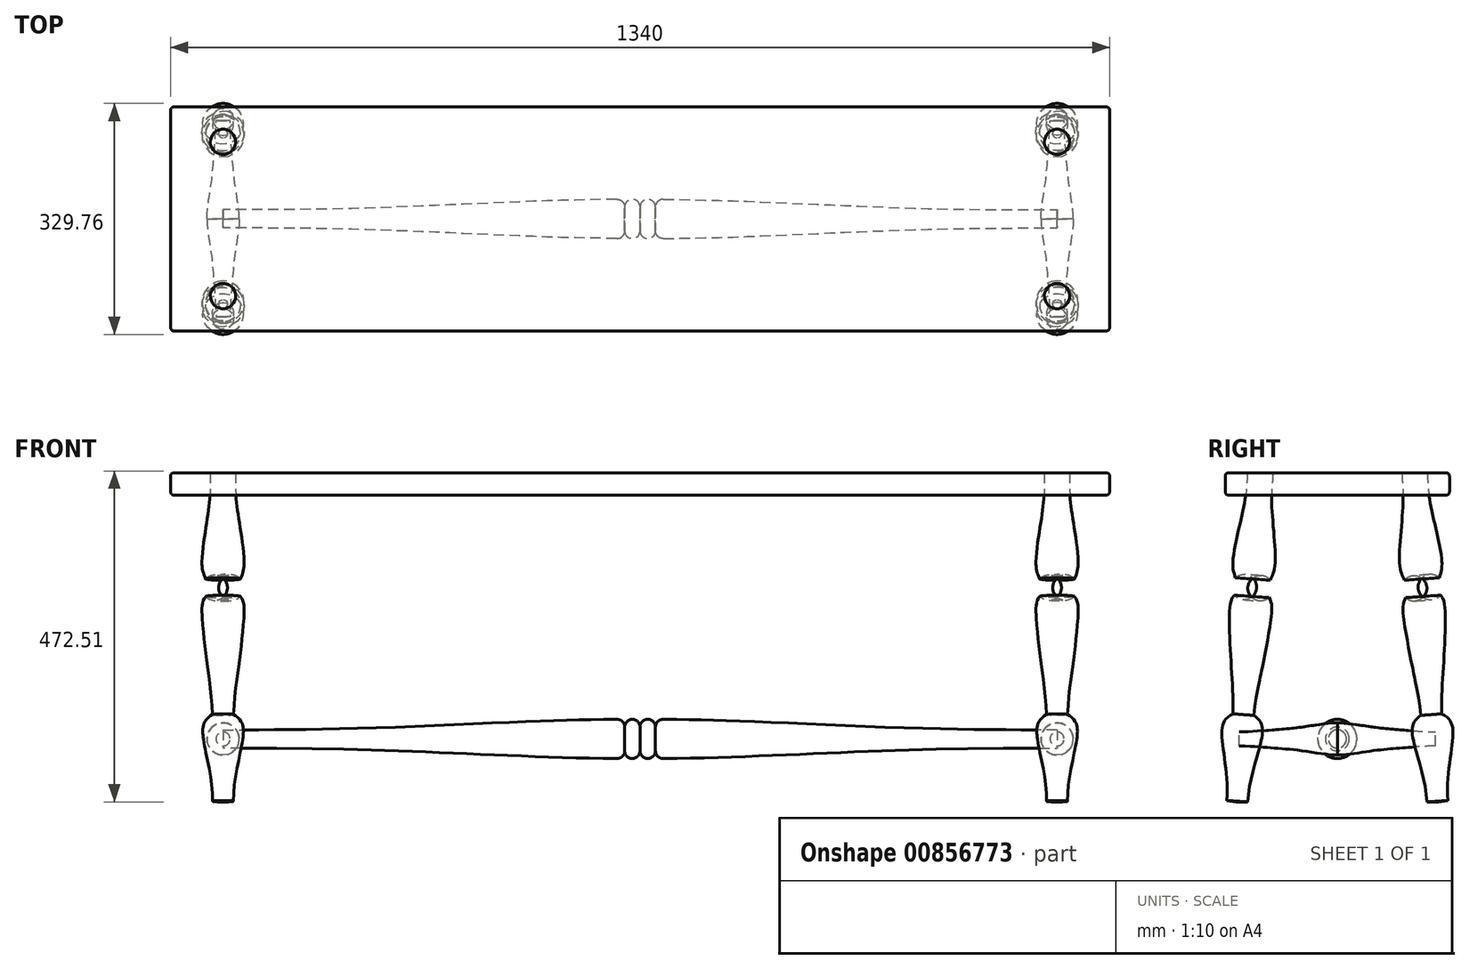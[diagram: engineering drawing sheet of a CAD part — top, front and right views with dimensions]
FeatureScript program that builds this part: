
annotation { "Feature Type Name" : "Feature", "Feature Type Description" : "" }
export const myFeature = defineFeature(function(context is Context, id is Id, definition is map)
    precondition{}
    {
        {
            assignVariable(context, id + "F0", {"name" : "height", "anyValue" : 470});
        }
        {
            assignVariable(context, id + "F1", {"name" : "topThick", "anyValue" : 32});
        }
        {
            assignVariable(context, id + "F2", {"name" : "endOverhang", "anyValue" : 75});
        }
        {
            var Q0;
            Q0=qCreatedBy(makeId("Top.planeOp"),FACE);
            cPlane(context, id + "F3", {"entities" : qUnion([Q0]), "cplaneType" : CPlaneType.OFFSET, "offset" : (getVariable(context, 'height')) * mm, "width" : 150 * mm, "height" : 150 * mm});
        }
        {
            var Q0;
            Q0=qCreatedBy(id+"F3.planeOp",FACE);
            var sketch = newSketch(context, id + "F4", { "sketchPlane" : qUnion([Q0])});
            skLineSegment(sketch, "E0.bottom", {"start": v(670, 160) * mm, "end": v(-670, 160) * mm});
            skLineSegment(sketch, "E0.top", {"start": v(670, -160) * mm, "end": v(-670, -160) * mm});
            skLineSegment(sketch, "E0.left", {"start": v(670, 160) * mm, "end": v(670, -160) * mm});
            skLineSegment(sketch, "E0.right", {"start": v(-670, 160) * mm, "end": v(-670, -160) * mm});
            skPoint(sketch, "E0.middle", {"position": v(0, 0) * mm});
            skSolve(sketch);
        }
        {
            var Q0;
            Q0=qSketchRegion(id+"F4",true);
            extrude(context, id + "F5", {"entities" : qUnion([Q0]), "oppositeDirection" : true, "depth" : (getVariable(context, 'topThick')) * mm, "offsetDistance" : 25 * mm});
        }
        {
            var Q0;
            Q0=makeQuery(id+"F5.opExtrude","CAP_FACE",FACE,{"disambiguationData":[OSD([sQuery(id+"F4.wireOp",EDGE,"E0.bottom"),sQuery(id+"F4.wireOp",EDGE,"E0.top"),sQuery(id+"F4.wireOp",EDGE,"E0.left"),sQuery(id+"F4.wireOp",EDGE,"E0.right")])],"isStart":true});
            var Q1;
            Q1=makeQuery(id+"F5.opExtrude","SWEPT_FACE",FACE,{"disambiguationData":[OSD([sQuery(id+"F4.wireOp",EDGE,"E0.left")])]});
            var Q2;
            Q2=makeQuery(id+"F5.opExtrude","SWEPT_FACE",FACE,{"disambiguationData":[OSD([sQuery(id+"F4.wireOp",EDGE,"E0.right")])]});
            var Q3;
            Q3=makeQuery(id+"F5.opExtrude","CAP_FACE",FACE,{"disambiguationData":[OSD([sQuery(id+"F4.wireOp",EDGE,"E0.bottom"),sQuery(id+"F4.wireOp",EDGE,"E0.top"),sQuery(id+"F4.wireOp",EDGE,"E0.left"),sQuery(id+"F4.wireOp",EDGE,"E0.right")])],"isStart":false});
            fillet(context, id + "F6", {"entities" : qUnion([Q0, Q1, Q2, Q3]), "radius" : 5 * mm, "tangentPropagation" : true, "allowEdgeOverflow" : false});
        }
        {
            var Q0;
            Q0=makeQuery(id+"F5.opExtrude","SWEPT_FACE",FACE,{"disambiguationData":[OSD([sQuery(id+"F4.wireOp",EDGE,"E0.left")])]});
            cPlane(context, id + "F7", {"entities" : qUnion([Q0]), "cplaneType" : CPlaneType.OFFSET, "offset" : (getVariable(context, 'endOverhang')) * mm, "oppositeDirection" : true, "width" : 150 * mm, "height" : 150 * mm});
        }
        {
            var Q0;
            Q0=qCreatedBy(id+"F7.planeOp",FACE);
            var sketch = newSketch(context, id + "F8", { "sketchPlane" : qUnion([Q0])});
            skLineSegment(sketch, "E1", {"start": v(-110, 470) * mm, "end": v(-142.87, 0) * mm});
            skLineSegment(sketch, "E2.0", {"start": v(-81.45, 448.19) * mm, "end": v(-112.8, 0) * mm, "construction": true});
            skLineSegment(sketch, "E3", {"start": v(-110, 528.62) * mm, "end": v(-110, 470) * mm, "construction": true});
            skPoint(sketch, "E4", {"position": v(-92, 470) * mm});
            skLineSegment(sketch, "E5", {"start": v(-95.66, 316.63) * mm, "end": v(-120.6, 318.37) * mm, "construction": true});
            skLineSegment(sketch, "E6", {"start": v(-122.35, 293.43) * mm, "end": v(-97.4, 291.69) * mm, "construction": true});
            skLineSegment(sketch, "E7", {"start": v(-119.2, 338.32) * mm, "end": v(-89.2, 336.22) * mm, "construction": true});
            skFitSpline(sketch, "E8", {"points": [v(-92, 470) * mm, v(-93.84, 428.77) * mm, v(-89.2, 336.22) * mm, v(-95.66, 316.63) * mm], "startDerivative": vector(-1.33, -110.65) * mm, "endDerivative": vector(-26.5, -67.26) * mm});
            skArc(sketch, "E9", {"start": v(-97.4, 291.69) * mm, "mid": v(-91.55, 303.8) * mm, "end": v(-95.66, 316.63) * mm});
            skPoint(sketch, "E10", {"position": v(-127.87, 0) * mm});
            skLineSegment(sketch, "E11", {"start": v(-142.87, 0) * mm, "end": v(-127.87, 0) * mm});
            skLineSegment(sketch, "E12", {"start": v(-135.89, 99.76) * mm, "end": v(-106.96, 97.73) * mm, "construction": true});
            skLineSegment(sketch, "E13", {"start": v(-119.18, 123.65) * mm, "end": v(-134.15, 124.7) * mm, "construction": true});
            skFitSpline(sketch, "E14", {"points": [v(-119.18, 123.65) * mm, v(-106.96, 97.73) * mm, v(-127.87, 0) * mm], "startDerivative": vector(88.45, -61.4) * mm, "endDerivative": vector(-11.95, -183.7) * mm});
            skLineSegment(sketch, "E15", {"start": v(-124.1, 268.5) * mm, "end": v(-94.16, 266.4) * mm, "construction": true});
            skFitSpline(sketch, "E16", {"points": [v(-97.4, 291.69) * mm, v(-94.16, 266.4) * mm, v(-106.08, 197.69) * mm, v(-119.18, 123.65) * mm], "startDerivative": vector(58.5, -103.3) * mm, "endDerivative": vector(-23.38, -210.4) * mm});
            skLineSegment(sketch, "E17", {"start": v(-110, 470) * mm, "end": v(-92, 470) * mm});
            skLineSegment(sketch, "E18", {"start": v(-93.84, 428.77) * mm, "end": v(-112.8, 430.1) * mm, "construction": true});
            skSolve(sketch);
        }
        {
            var Q0;
            Q0=qSketchRegion(id+"F8",true);
            var Q1;
            Q1=sQuery(id+"F8.wireOp",EDGE,"E1");
            revolve(context, id + "F9", {"entities" : qUnion([Q0]), "axis" : qUnion([Q1]), "revolveType" : RevolveType.FULL});
        }
        {
            var Q0;
            Q0=qCreatedBy(id+"F7.planeOp",FACE);
            var sketch = newSketch(context, id + "F10", { "sketchPlane" : qUnion([Q0])});
            skLineSegment(sketch, "E19.bottom", {"start": v(-133.48, 475.27) * mm, "end": v(-82.36, 475.27) * mm});
            skLineSegment(sketch, "E19.top", {"start": v(-133.48, 470) * mm, "end": v(-82.36, 470) * mm});
            skLineSegment(sketch, "E19.left", {"start": v(-133.48, 475.27) * mm, "end": v(-133.48, 470) * mm});
            skLineSegment(sketch, "E19.right", {"start": v(-82.36, 475.27) * mm, "end": v(-82.36, 470) * mm});
            skSolve(sketch);
        }
        {
            var Q0;
            Q0=makeQuery(id+"F10.imprint","IMPRINT",FACE,{"disambiguationData":[TD([[makeQuery(id+"F10.imprint","IMPRINT",EDGE,{"derivedFrom":sQuery(id+"F10.wireOp",EDGE,"E19.bottom")}),-1.0]])]});
            extrude(context, id + "F11", {"entities" : qUnion([Q0]), "operationType" : NewBodyOperationType.REMOVE, "endBound" : BoundingType.THROUGH_ALL, "oppositeDirection" : true, "depth" : 25 * mm, "offsetDistance" : 25 * mm, "hasSecondDirection" : true, "secondDirectionOppositeDirection" : false, "secondDirectionDepth" : 25 * mm});
        }
        {
            var Q0;
            Q0=makeQuery(id+"F9.opRevolve","SWEPT_BODY",BODY,{"disambiguationData":[OSD([sQuery(id+"F8.wireOp",EDGE,"E1"),sQuery(id+"F8.wireOp",EDGE,"E8"),sQuery(id+"F8.wireOp",EDGE,"E9"),sQuery(id+"F8.wireOp",EDGE,"E11"),sQuery(id+"F8.wireOp",EDGE,"E14"),sQuery(id+"F8.wireOp",EDGE,"E16"),sQuery(id+"F8.wireOp",EDGE,"E17")])]});
            var Q1;
            Q1=qCreatedBy(makeId("Front.planeOp"),FACE);
            mirror(context, id + "F12", {"entities" : qUnion([Q0]), "mirrorPlane" : qUnion([Q1])});
        }
        {
            var Q0;
            Q0=qCreatedBy(id+"F7.planeOp",FACE);
            var sketch = newSketch(context, id + "F13", { "sketchPlane" : qUnion([Q0])});
            skLineSegment(sketch, "E20", {"start": v(-140, 90) * mm, "end": v(140, 90) * mm});
            skLineSegment(sketch, "E21", {"start": v(-140, 90) * mm, "end": v(-140, 80) * mm});
            skLineSegment(sketch, "E22", {"start": v(140, 90) * mm, "end": v(140, 80) * mm});
            skFitSpline(sketch, "E23", {"points": [v(-140, 80) * mm, v(-90, 77) * mm, v(-50, 73) * mm, v(0, 67) * mm], "startDerivative": vector(196.9, -5.62) * mm, "endDerivative": vector(98.9, 2.93) * mm});
            skFitSpline(sketch, "E24.MirrorCS", {"points": [v(140, 80) * mm, v(90, 77) * mm, v(50, 73) * mm, v(0, 67) * mm], "startDerivative": vector(-196.9, -5.62) * mm, "endDerivative": vector(-98.9, 2.93) * mm});
            skLineSegment(sketch, "E25", {"start": v(0, 67) * mm, "end": v(0, 90) * mm, "construction": true});
            skLineSegment(sketch, "E26", {"start": v(-90, 77) * mm, "end": v(-90, 90) * mm, "construction": true});
            skLineSegment(sketch, "E27", {"start": v(-50, 73) * mm, "end": v(-50, 90) * mm, "construction": true});
            skSolve(sketch);
        }
        {
            var Q0;
            Q0=makeQuery(id+"F13.imprint","IMPRINT",FACE,{"disambiguationData":[TD([[makeQuery(id+"F13.imprint","IMPRINT",EDGE,{"derivedFrom":sQuery(id+"F13.wireOp",EDGE,"E20")}),-1.0]])]});
            var Q1;
            Q1=sQuery(id+"F13.wireOp",EDGE,"E20");
            revolve(context, id + "F14", {"entities" : qUnion([Q0]), "axis" : qUnion([Q1]), "revolveType" : RevolveType.FULL});
        }
        {
            var Q0;
            Q0=makeQuery(id+"F14.opRevolve","SWEPT_BODY",BODY,{"disambiguationData":[OSD([sQuery(id+"F13.wireOp",EDGE,"E20"),sQuery(id+"F13.wireOp",EDGE,"E21"),sQuery(id+"F13.wireOp",EDGE,"E22"),sQuery(id+"F13.wireOp",EDGE,"E23"),sQuery(id+"F13.wireOp",EDGE,"E24.MirrorCS")])]});
            var Q1;
            Q1=makeQuery(id+"F9.opRevolve","SWEPT_BODY",BODY,{"disambiguationData":[OSD([sQuery(id+"F8.wireOp",EDGE,"E1"),sQuery(id+"F8.wireOp",EDGE,"E8"),sQuery(id+"F8.wireOp",EDGE,"E9"),sQuery(id+"F8.wireOp",EDGE,"E11"),sQuery(id+"F8.wireOp",EDGE,"E14"),sQuery(id+"F8.wireOp",EDGE,"E16"),sQuery(id+"F8.wireOp",EDGE,"E17")])]});
            var Q2;
            Q2=makeQuery(id+"F12.opPattern","COPY",BODY,{"derivedFrom":makeQuery(id+"F9.opRevolve","SWEPT_BODY",BODY,{"disambiguationData":[OSD([sQuery(id+"F8.wireOp",EDGE,"E1"),sQuery(id+"F8.wireOp",EDGE,"E8"),sQuery(id+"F8.wireOp",EDGE,"E9"),sQuery(id+"F8.wireOp",EDGE,"E11"),sQuery(id+"F8.wireOp",EDGE,"E14"),sQuery(id+"F8.wireOp",EDGE,"E16"),sQuery(id+"F8.wireOp",EDGE,"E17")])]}),"instanceName":"1"});
            var Q3;
            Q3=qCreatedBy(makeId("Right.planeOp"),FACE);
            mirror(context, id + "F15", {"entities" : qUnion([Q0, Q1, Q2]), "mirrorPlane" : qUnion([Q3])});
        }
        {
            var Q0;
            Q0=qCreatedBy(makeId("Front.planeOp"),FACE);
            var sketch = newSketch(context, id + "F16", { "sketchPlane" : qUnion([Q0])});
            skLineSegment(sketch, "E28", {"start": v(-595, 90) * mm, "end": v(595, 90) * mm});
            skLineSegment(sketch, "E29", {"start": v(595, 90) * mm, "end": v(595, 77) * mm});
            skLineSegment(sketch, "E30", {"start": v(-595, 90) * mm, "end": v(-595, 77) * mm});
            skLineSegment(sketch, "E31", {"start": v(0, 90) * mm, "end": v(0, 62) * mm, "construction": true});
            skLineSegment(sketch, "E32", {"start": v(-154, 90) * mm, "end": v(-154, 65) * mm, "construction": true});
            skLineSegment(sketch, "E33", {"start": v(-404.36, 75) * mm, "end": v(-404.36, 90) * mm, "construction": true});
            skFitSpline(sketch, "E34", {"points": [v(-595, 77) * mm, v(-404.36, 75) * mm, v(-154, 65) * mm, v(-33.16, 62) * mm], "startDerivative": vector(549.15, 0.22) * mm, "endDerivative": vector(482.3, -7.03) * mm});
            skArc(sketch, "E35", {"start": v(-22, 73) * mm, "mid": v(-11, 62) * mm, "end": v(0, 73) * mm});
            skLineSegment(sketch, "E36", {"start": v(-35.8, 73) * mm, "end": v(34.63, 73) * mm, "construction": true});
            skArc(sketch, "E37", {"start": v(-33.16, 62) * mm, "mid": v(-25.28, 65.17) * mm, "end": v(-22, 73) * mm});
            skLineSegment(sketch, "E38", {"start": v(0, 62) * mm, "end": v(-30.4, 62) * mm, "construction": true});
            skArc(sketch, "E39.MirrorCS", {"start": v(22, 73) * mm, "mid": v(11, 62) * mm, "end": v(0, 73) * mm});
            skArc(sketch, "E40.MirrorCS", {"start": v(33.16, 62) * mm, "mid": v(25.28, 65.17) * mm, "end": v(22, 73) * mm});
            skFitSpline(sketch, "E41.MirrorCS", {"points": [v(595, 77) * mm, v(404.36, 75) * mm, v(154, 65) * mm, v(33.16, 62) * mm], "startDerivative": vector(-549.15, 0.22) * mm, "endDerivative": vector(-482.3, -7.03) * mm});
            skSolve(sketch);
        }
        {
            var Q0;
            Q0=qSketchRegion(id+"F16",true);
            var Q1;
            Q1=sQuery(id+"F16.wireOp",EDGE,"E28");
            revolve(context, id + "F17", {"entities" : qUnion([Q0]), "axis" : qUnion([Q1]), "revolveType" : RevolveType.FULL});
        }
    });
